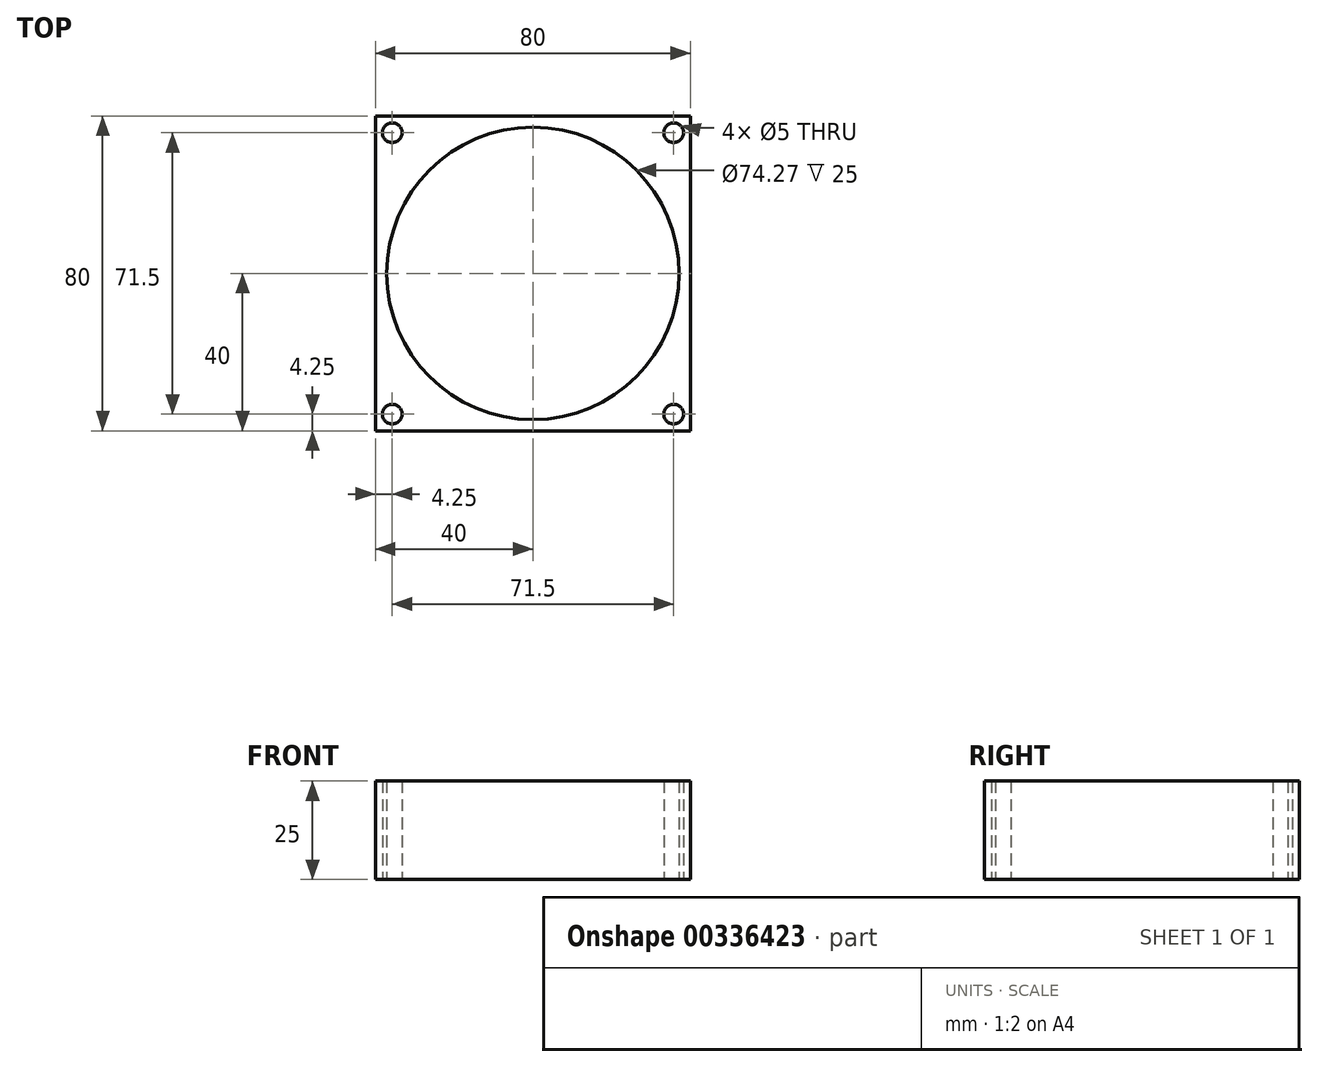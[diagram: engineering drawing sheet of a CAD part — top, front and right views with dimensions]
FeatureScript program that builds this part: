
annotation { "Feature Type Name" : "Feature", "Feature Type Description" : "" }
export const myFeature = defineFeature(function(context is Context, id is Id, definition is map)
    precondition{}
    {
        {
            var Q0;
            Q0=qCreatedBy(makeId("Top.planeOp"),FACE);
            var sketch = newSketch(context, id + "F0", { "sketchPlane" : qUnion([Q0])});
            skCircle(sketch, "E0", {"center": v(0, 0) * mm, "radius": 37.14 * mm});
            skLineSegment(sketch, "E1.bottom", {"start": v(40, -40) * mm, "end": v(-40, -40) * mm});
            skLineSegment(sketch, "E1.top", {"start": v(40, 40) * mm, "end": v(-40, 40) * mm});
            skLineSegment(sketch, "E1.left", {"start": v(40, -40) * mm, "end": v(40, 40) * mm});
            skLineSegment(sketch, "E1.right", {"start": v(-40, -40) * mm, "end": v(-40, 40) * mm});
            skLineSegment(sketch, "E2", {"start": v(0, 40) * mm, "end": v(0, -40) * mm, "construction": true});
            skLineSegment(sketch, "E3", {"start": v(-40, 0) * mm, "end": v(40, 0) * mm, "construction": true});
            skCircle(sketch, "E4", {"center": v(-35.75, 35.75) * mm, "radius": 2.5 * mm});
            skCircle(sketch, "E5.MirrorC", {"center": v(-35.75, -35.75) * mm, "radius": 2.5 * mm});
            skCircle(sketch, "E6.MirrorC", {"center": v(35.75, 35.75) * mm, "radius": 2.5 * mm});
            skCircle(sketch, "E7.MirrorC", {"center": v(35.75, -35.75) * mm, "radius": 2.5 * mm});
            skSolve(sketch);
        }
        {
            var Q0;
            Q0 = qSketchRegion(id + "F0", true);
            extrude(context, id + "F1", {"entities" : qUnion([Q0]), "depth" : 25 * mm});
        }
    });
